# Revit family: PRD_AR_ShwrFttngsPckg_ShowerPanel_F5SM2014-16_F5SM2020-21_F5SM2024_26
name_source: partatom
category: Plumbing Fixtures
revit_build: Autodesk Revit 2018 (Build: 20190510_1515(x64)
units: mm (PartAtom-declared; Revit-internal decimal feet)

## family parameters
Cut with Voids When Loaded = No
Host = Face
OmniClass Number = 23.45.05.14.17
OmniClass Title = Showers
Part Type = Normal
Room Calculation Point = No
Round Connector Dimension = Use Diameter
Shared = No

## types (8) — shared parameters
AdditionalConnections = No
AdjustableFlowTime = Yes
AssetType = Fixed
CasingMaterial = PRD_AR_StainlessSteel_SatinFinished_Dark
Category = Pr_40_20_87_75, Shower fittings package
Circulation = No
ConnectionWithPayWaterDispenser = Not possible
Default Elevation = 1500 mm  [stored 4.92126 ft]
DurationUnit = year
FittingMaterial = PRD_AR_ChromatedBrass_HighPolished
FlowColdWater = 0.2 L/s
FlowHotWater = 0.2 L/s
FunctionalPrinciple = Hydraulic self-closing
IfcExportAs = IfcSanitaryTerminalType
IfcExportType = SHOWER
InletSize = G-1-2-A
Manufacturer = KWC Group AG
ManufacturerName = KWC Group AG
ManufacturerURL = www.kwc.com
MaximumFlowTime = 35.00 seconds
MinimumFlowTime = 5.00 seconds
NBSDescription = Shower fittings package
NBSReference = 45-35-70/330
NominalHeight = 1160 mm  [stored 3.80577 ft]
NominalWidth = 235 mm  [stored 0.770997 ft]
PositionOfWaterConnection = From top / backside
ProductInformation = https://pim.kwc.com
ProtectiveShutdown = No
ShowerType = Individual
SoundInsulation = No
TailorMade = No
ThermalDisinfection = No
TubeMaterial = PRD_AR_StainlessSteel_SatinFinished
TypeOfMixing = With mixing
TypeOfMounting = Wall mounting
TypeOfOperation = Manual operation
TypeOfShower = Shower panel
URL = www.kwc.com
Uniclass2015Code = Pr_40_20_87_75
Uniclass2015Title = Shower fittings package
Uniclass2015Version = Products v1.17
Version = 1
WarrantyDurationUnit = year
zero-valued in all types: DrainSize

## per-type parameters (varying)
- F5SM2020: BIMObjectName=PRD_AR_ShowerFittingsPackage_ShowerPanel_F5SM2020; BodyMaterial=PRD_AR_StainlessSteel_SatinFinished; Color=stainless steel; ColorCasing=Yes; Description=F5S Mix shower panel made of stainless steel for wall mounting with DN 15 self-closing single control mixer and connecting nozzles for the shower head. FRAMIC self-closing mixing cartridge, hydraulically controlled, low maintenance and stagnation free, with ceramic disc technology, self closing, flow pressure independent due to the medium-independent design. Stepless adjustment of flow duration. With adjustable, turn-proof temperature stop. For conection to hot and cold water. All-metal construction, visible parts high-polished or chrome-plated. Connecting nozzles for the required additional DN 15 KWC shower head with pre-fitted flow regulator 9.0 l/min. Housing made of stainless steel with raised function surface and plastic cover caps. Connecting hoses with lockable water volume control with backflow preventer and strainer.; Features=stainless steel, with self-closing single control mixer; Finish=satin finished; GrossWeight=9.00 kg; HandShowerFittingOffset=0 mm  [stored 0 ft]; HandShowerVisibility=No; HasTray=No; HygieneFlushing=No; IntegralAccessories=shower head to be ordered separately; Material=stainless steel; MaterialCode=1.4301; MinimumFlowPressure=1.50 bar; ModelNumber=2030054248; Name=Shower Panel F5SM2020; NetWeight=8.55 kg; NominalDepth=90 mm  [stored 0.295276 ft]; ShelfVisibility=No; ShowerPipeDraining=No; ShowerPipeDrainingVisibility=No; Size=235 x 1160 x 90 mm (W x H x D); VolumeFlowRate=0.15 L/s at 3 bar
- F5SM2021: BIMObjectName=PRD_AR_ShowerFittingsPackage_ShowerPanel_F5SM2021; BodyMaterial=PRD_AR_StainlessSteel_SatinFinished; Color=stainless steel; ColorCasing=Yes; Description=F5S Mix shower panel made of stainless steel for wall mounting with DN 15 self-closing single control mixer and a hand shower fitting. FRAMIC self-closing mixing cartridge, hydraulically controlled, low maintenance and stagnation free, with ceramic disc technology, self closing, flow pressure independent due to the medium-independent design. Stepless adjustment of flow duration. With adjustable, turn-proof temperature stop. For conection to hot and cold water. All-metal construction, visible parts high-polished or chrome-plated. Pre-fitted chrome-plated brass shower pole with height-adjustable hand shower holder and chrome-plated plastic hand shower, shower head with rain jet, diameter 110 mm, shower hose 900 mm. Housing made of stainless steel with raised function surface and plastic cover caps. Connecting hoses with lockable water volume control with backflow preventer and strainer.; Features=stainless steel, with self-closing single control mixer and a hand shower fitting; Finish=satin finished; GrossWeight=14.00 kg; HandShowerFittingOffset=0 mm  [stored 0 ft]; HandShowerVisibility=Yes; HasTray=No; HygieneFlushing=No; Material=stainless steel; MaterialCode=1.4301; MinimumFlowPressure=1.00 bar; ModelNumber=2030056548; Name=Shower Panel F5SM2021; NetWeight=12.00 kg; NominalDepth=90 mm  [stored 0.295276 ft]; ShelfVisibility=No; ShowerPipeDraining=No; ShowerPipeDrainingVisibility=No; Size=235 x 1160 x 90 mm (W x H x D)
- F5SM2024: BIMObjectName=PRD_AR_ShowerFittingsPackage_ShowerPanel_F5SM2024; BodyMaterial=PRD_AR_MineralMaterial_Chromed; Color=alpine white; ColorCasing=No; Description=F5S Mix shower panel made of mineral material for wall mounting with DN 15 self-closing single control mixer and connecting nozzles for the shower head. FRAMIC self-closing mixing cartridge, hydraulically controlled, low maintenance and stagnation free, with ceramic disc technology, self closing, flow pressure independent due to the medium-independent design. Stepless adjustment of flow duration. With adjustable, turn-proof temperature stop. For conection to hot and cold water. All-metal construction, visible parts high-polished or chrome-plated. Connecting nozzles for the required additional DN 15 KWC shower head with pre-fitted flow regulator 9.0 l/min. Housing with raised function surface made of MIRANIT resin-bonded mineral material with pore-free smooth surface (temperature-resistant up to 80°C), Alpine white colour. Connecting hoses with lockable water volume control with backflow preventer and strainer.; Features=mineral material, with self-closing single control mixer; Finish=chromed; GrossWeight=16.50 kg; HandShowerFittingOffset=10 mm  [stored 0.0328084 ft]; HandShowerVisibility=No; HasTray=No; HygieneFlushing=No; IntegralAccessories=shower head to be ordered separately; Material=mineral material; MaterialCode=Miranit; MinimumFlowPressure=1.50 bar; ModelNumber=2030056549; Name=Shower Panel F5SM2024; NetWeight=15.00 kg; NominalDepth=100 mm  [stored 0.328084 ft]; ShelfVisibility=No; ShowerPipeDraining=No; ShowerPipeDrainingVisibility=No; Size=235 x 1160 x 100 mm (W x H x D); VolumeFlowRate=0.15 L/s at 3 bar
- F5SM2025: BIMObjectName=PRD_AR_ShowerFittingsPackage_ShowerPanel_F5SM2025; BodyMaterial=PRD_AR_MineralMaterial_Chromed; Color=alpine white; ColorCasing=No; Description=F5S Mix shower panel made of mineral material for wall mounting with DN 15 self-closing single control mixer and a hand shower fitting. FRAMIC self-closing mixing cartridge, hydraulically controlled, low maintenance and stagnation free, with ceramic disc technology, self closing, flow pressure independent due to the medium-independent design. Stepless adjustment of flow duration. With adjustable, turn-proof temperature stop. For conection to hot and cold water. All-metal construction, visible parts high-polished or chrome-plated. Pre-fitted chrome-plated brass shower pole with height-adjustable hand shower holder and chrome-plated plastic hand shower, shower head with rain jet, diameter 110 mm, shower hose 900 mm. Housing with raised function surface made of MIRANIT resin-bonded mineral material with pore-free smooth surface (temperature-resistant up to 80°C), Alpine white colour. Connecting hoses with lockable water volume control with backflow preventer and strainer.; Features=mineral material, with self-closing single control mixer and a hand shower fitting; Finish=chromed; GrossWeight=16.50 kg; HandShowerFittingOffset=10 mm  [stored 0.0328084 ft]; HandShowerVisibility=Yes; HasTray=No; HygieneFlushing=No; Material=mineral material; MaterialCode=Miranit; MinimumFlowPressure=1.00 bar; ModelNumber=2030056550; Name=Shower Panel F5SM2025; NetWeight=15.00 kg; NominalDepth=100 mm  [stored 0.328084 ft]; ShelfVisibility=No; ShowerPipeDraining=No; ShowerPipeDrainingVisibility=No; Size=235 x 1160 x 100 mm (W x H x D)
- F5SM2026: BIMObjectName=PRD_AR_ShowerFittingsPackage_ShowerPanel_F5SM2026; BodyMaterial=PRD_AR_MineralMaterial_Chromed; Color=alpine white; ColorCasing=No; Description=F5S Mix shower panel made of mineral material for wall mounting with DN 15 self-closing single control mixer and connecting nozzles for the shower head. FRAMIC self-closing mixing cartridge, hydraulically controlled, low maintenance and stagnation free, with ceramic disc technology, self closing, flow pressure independent due to the medium-independent design. Stepless adjustment of flow duration. With adjustable, turn-proof temperature stop. For conection to hot and cold water. All-metal construction, visible parts high-polished or chrome-plated. Connecting nozzles for the required additional DN 15 KWC shower head with pre-fitted flow regulator 9.0 l/min. Housing with raised function surface and seamless moulded shower gel shelf made of MIRANIT resin-bonded mineral material with pore-free smooth surface (temperature-resistant up to 80°C), Alpine white colour. Connecting hoses with lockable water volume control with backflow preventer and strainer.; Features=mineral material, with self-closing single control mixer; Finish=chromed; GrossWeight=16.50 kg; HandShowerFittingOffset=10 mm  [stored 0.0328084 ft]; HandShowerVisibility=No; HasTray=Yes; IntegralAccessories=shower head to be ordered separately; Material=mineral material; MaterialCode=Miranit; MinimumFlowPressure=1.50 bar; ModelNumber=2030056552; Name=Shower Panel F5SM2026; NetWeight=15.00 kg; NominalDepth=100 mm  [stored 0.328084 ft]; ShelfVisibility=Yes; ShowerPipeDraining=No; ShowerPipeDrainingVisibility=No; Size=235 x 1160 x 100 mm (W x H x D); VolumeFlowRate=0.15 L/s at 3 bar
- F5SM2014: BIMObjectName=PRD_AR_ShowerFittingsPackage_ShowerPanel_F5SM2014; BodyMaterial=PRD_AR_StainlessSteel_SatinFinished; Color=stainless steel; ColorCasing=Yes; Description=F5S Mix shower panel made of stainless steel for wall mounting with DN 15 self-closing single control mixer and connecting nozzles for the shower head. FRAMIC self-closing mixing cartridge, hydraulically controlled, low maintenance and stagnation free, with ceramic disc technology, self closing, flow pressure independent due to the medium-independent design. Stepless adjustment of flow duration. With adjustable, turn-proof temperature stop. For conection to hot and cold water. All-metal construction, visible parts high-polished or chrome-plated. Connecting nozzles for the required additional DN 15 KWC shower head with pre-fitted flow regulator 9.0 l/min. Housing made of stainless steel with raised function surface and plastic cover caps. Connecting hoses with lockable water volume control with backflow preventer and strainer. Version with automatic shower pipe draining.; Features=stainless steel, with self-closing single control mixer; Finish=satin finished; GrossWeight=14.00 kg; HandShowerFittingOffset=0 mm  [stored 0 ft]; HandShowerVisibility=No; HasTray=No; HygieneFlushing=No; IntegralAccessories=shower head to be ordered separately; Material=stainless steel; MaterialCode=1.4301; MinimumFlowPressure=1.50 bar; ModelNumber=2030056581; Name=Shower Panel F5SM2014; NetWeight=12.00 kg; NominalDepth=90 mm  [stored 0.295276 ft]; ShelfVisibility=No; ShowerPipeDraining=Yes; ShowerPipeDrainingVisibility=Yes; Size=235 x 1160 x 90 mm (W x H x D); VolumeFlowRate=0.15 L/s at 3 bar
- F5SM2015: BIMObjectName=PRD_AR_ShowerFittingsPackage_ShowerPanel_F5SM2015; BodyMaterial=PRD_AR_MineralMaterial_Chromed; Color=alpine white; ColorCasing=No; Description=F5S Mix shower panel made of mineral material for wall mounting with DN 15 self-closing single control mixer and connecting nozzles for the shower head. FRAMIC self-closing mixing cartridge, hydraulically controlled, low maintenance and stagnation free, with ceramic disc technology, self closing, flow pressure independent due to the medium-independent design. Stepless adjustment of flow duration. With adjustable, turn-proof temperature stop. For conection to hot and cold water. All-metal construction, visible parts high-polished or chrome-plated. Connecting nozzles for the required additional DN 15 KWC shower head with pre-fitted flow regulator 9.0 l/min. Housing with raised function surface made of MIRANIT resin-bonded mineral material with pore-free smooth surface (temperature-resistant up to 80°C), Alpine white colour. Connecting hoses with lockable water volume control with backflow preventer and strainer. Version with automatic shower pipe draining.; Features=mineral material, with self-closing single control mixer; Finish=chromed; GrossWeight=16.50 kg; HandShowerFittingOffset=10 mm  [stored 0.0328084 ft]; HandShowerVisibility=No; HasTray=No; HygieneFlushing=No; IntegralAccessories=shower head to be ordered separately; Material=mineral material; MaterialCode=Miranit; MinimumFlowPressure=1.50 bar; ModelNumber=2030056584; Name=Shower Panel F5SM2015; NetWeight=15.00 kg; NominalDepth=100 mm  [stored 0.328084 ft]; ShelfVisibility=No; ShowerPipeDraining=Yes; ShowerPipeDrainingVisibility=Yes; Size=235 x 1160 x 100 mm (W x H x D); VolumeFlowRate=0.15 L/s at 3 bar
- F5SM2016: BIMObjectName=PRD_AR_ShowerFittingsPackage_ShowerPanel_F5SM2016; BodyMaterial=PRD_AR_MineralMaterial_Chromed; Color=alpine white; ColorCasing=No; Description=F5S Mix shower panel made of mineral material for wall mounting with DN 15 self-closing single control mixer and connecting nozzles for the shower head. FRAMIC self-closing mixing cartridge, hydraulically controlled, low maintenance and stagnation free, with ceramic disc technology, self closing, flow pressure independent due to the medium-independent design. Stepless adjustment of flow duration. With adjustable, turn-proof temperature stop. For conection to hot and cold water. All-metal construction, visible parts high-polished or chrome-plated. Connecting nozzles for the required additional DN 15 KWC shower head with pre-fitted flow regulator 9.0 l/min. Housing with raised function surface and seamless moulded shower gel shelf made of MIRANIT resin-bonded mineral material with pore-free smooth surface (temperature-resistant up to 80°C), Alpine white colour. Connecting hoses with lockable water volume control with backflow preventer and strainer. Version with automatic shower pipe draining.; Features=mineral material, with self-closing single control mixer; Finish=chromed; GrossWeight=16.50 kg; HandShowerFittingOffset=10 mm  [stored 0.0328084 ft]; HandShowerVisibility=No; HasTray=Yes; HygieneFlushing=No; IntegralAccessories=shower head to be ordered separately; Material=mineral material; MaterialCode=Miranit; MinimumFlowPressure=1.50 bar; ModelNumber=2030056588; Name=Shower Panel F5SM2016; NetWeight=15.00 kg; NominalDepth=100 mm  [stored 0.328084 ft]; ShelfVisibility=Yes; ShowerPipeDraining=Yes; ShowerPipeDrainingVisibility=Yes; Size=235 x 1160 x 100 mm (W x H x D); VolumeFlowRate=0.15 L/s at 3 bar

note: column(s) folded — value = type name in every type: Model, ModelReference

note: [stored X ft] marks values corroborated as IEEE doubles in the binary element streams (Revit-internal decimal feet)

## geometry (parser evidence)
native form markers: Extrusion x2, Sweep x4
no freeform markers — native parametric forms only
